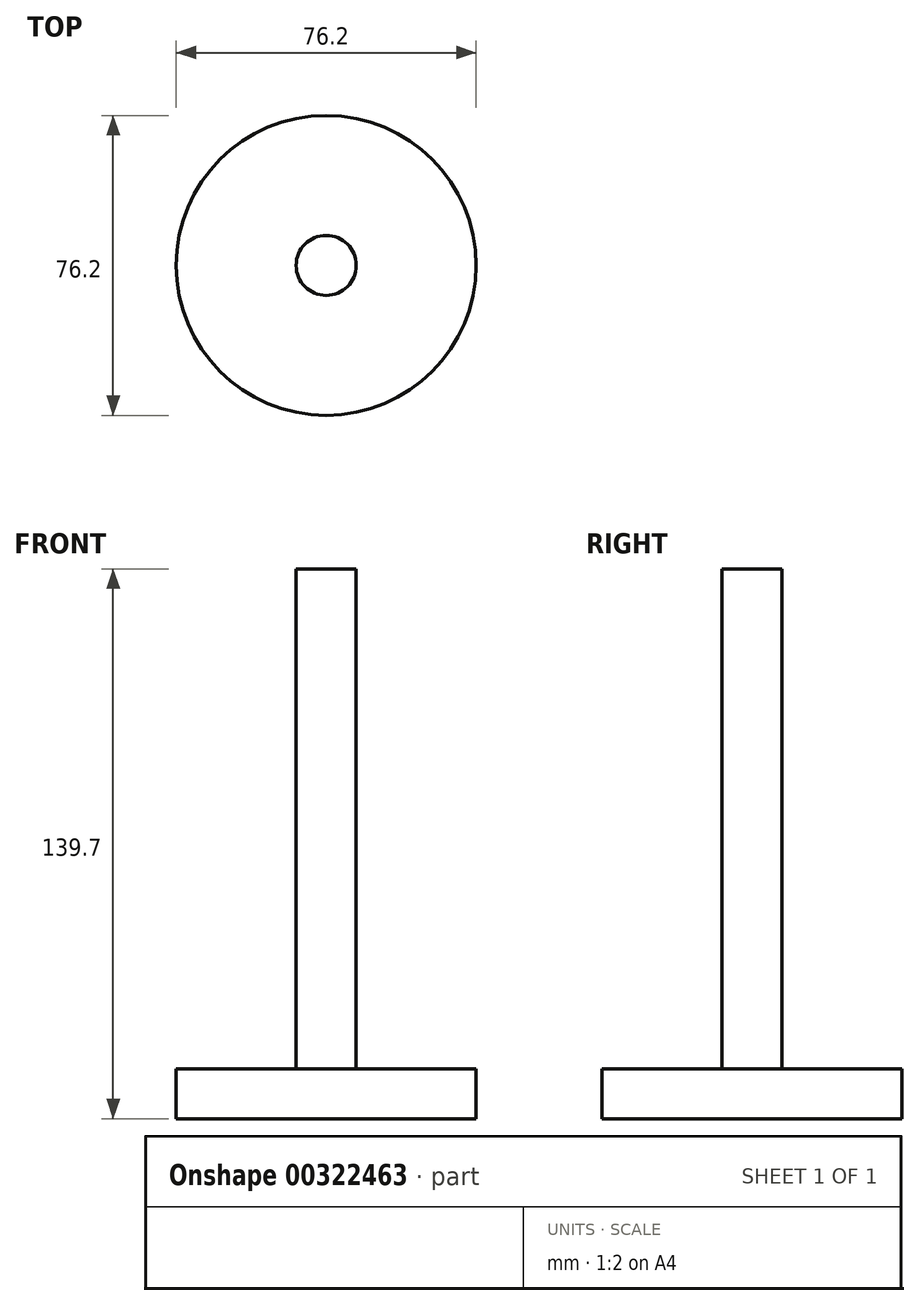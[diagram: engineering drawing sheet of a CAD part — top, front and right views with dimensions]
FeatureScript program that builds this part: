
annotation { "Feature Type Name" : "Feature", "Feature Type Description" : "" }
export const myFeature = defineFeature(function(context is Context, id is Id, definition is map)
    precondition{}
    {
        {
            var Q0;
            Q0=qCreatedBy(makeId("Top.planeOp"),FACE);
            var sketch = newSketch(context, id + "F0", { "sketchPlane" : qUnion([Q0])});
            skCircle(sketch, "E0", {"center": v(0, 0) * mm, "radius": 7.62 * mm});
            skSolve(sketch);
        }
        {
            var Q0;
            Q0 = qSketchRegion(id + "F0", true);
            extrude(context, id + "F1", {"entities" : qUnion([Q0]), "depth" : 139.7 * mm});
        }
        {
            var Q0;
            Q0=qCreatedBy(makeId("Top.planeOp"),FACE);
            var sketch = newSketch(context, id + "F2", { "sketchPlane" : qUnion([Q0])});
            skCircle(sketch, "E1", {"center": v(0, 0) * mm, "radius": 38.1 * mm});
            skSolve(sketch);
        }
        {
            var Q0;
            Q0=makeQuery(id+"F2.imprint","IMPRINT",FACE,{"disambiguationData":[TD([[makeQuery(id+"F2.imprint","IMPRINT",EDGE,{"derivedFrom":sQuery(id+"F2.wireOp",EDGE,"E1")}),1.0]])]});
            extrude(context, id + "F3", {"entities" : qUnion([Q0]), "operationType" : NewBodyOperationType.ADD, "depth" : 12.7 * mm});
        }
    });
